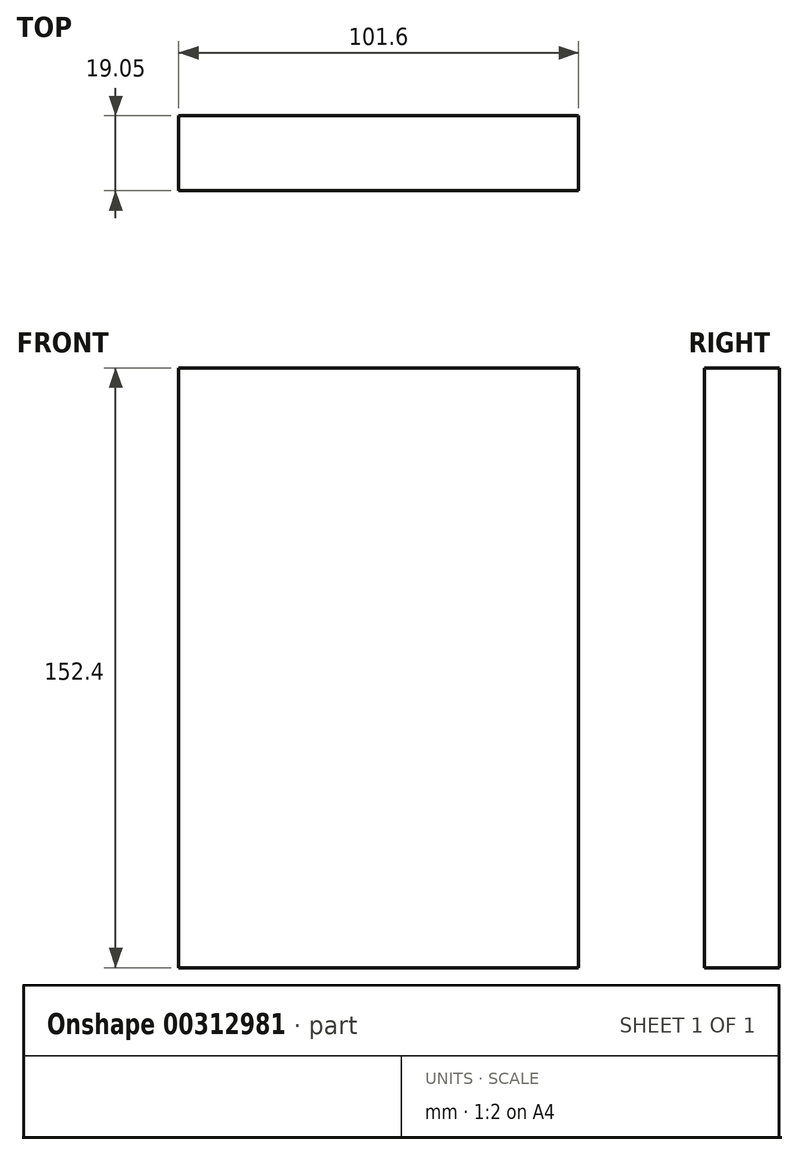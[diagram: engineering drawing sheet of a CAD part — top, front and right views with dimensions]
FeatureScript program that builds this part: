
annotation { "Feature Type Name" : "Feature", "Feature Type Description" : "" }
export const myFeature = defineFeature(function(context is Context, id is Id, definition is map)
    precondition{}
    {
        {
            var Q0;
            Q0=qCreatedBy(makeId("Front.planeOp"),FACE);
            var sketch = newSketch(context, id + "F0", { "sketchPlane" : qUnion([Q0])});
            skLineSegment(sketch, "E0.bottom", {"start": v(50.8, 76.2) * mm, "end": v(-50.8, 76.2) * mm});
            skLineSegment(sketch, "E0.top", {"start": v(50.8, -76.2) * mm, "end": v(-50.8, -76.2) * mm});
            skLineSegment(sketch, "E0.left", {"start": v(50.8, 76.2) * mm, "end": v(50.8, -76.2) * mm});
            skLineSegment(sketch, "E0.right", {"start": v(-50.8, 76.2) * mm, "end": v(-50.8, -76.2) * mm});
            skPoint(sketch, "E0.middle", {"position": v(0, 0) * mm});
            skSolve(sketch);
        }
        {
            var Q0;
            Q0 = qSketchRegion(id + "F0", true);
            extrude(context, id + "F1", {"entities" : qUnion([Q0]), "depth" : 19.05 * mm});
        }
    });
